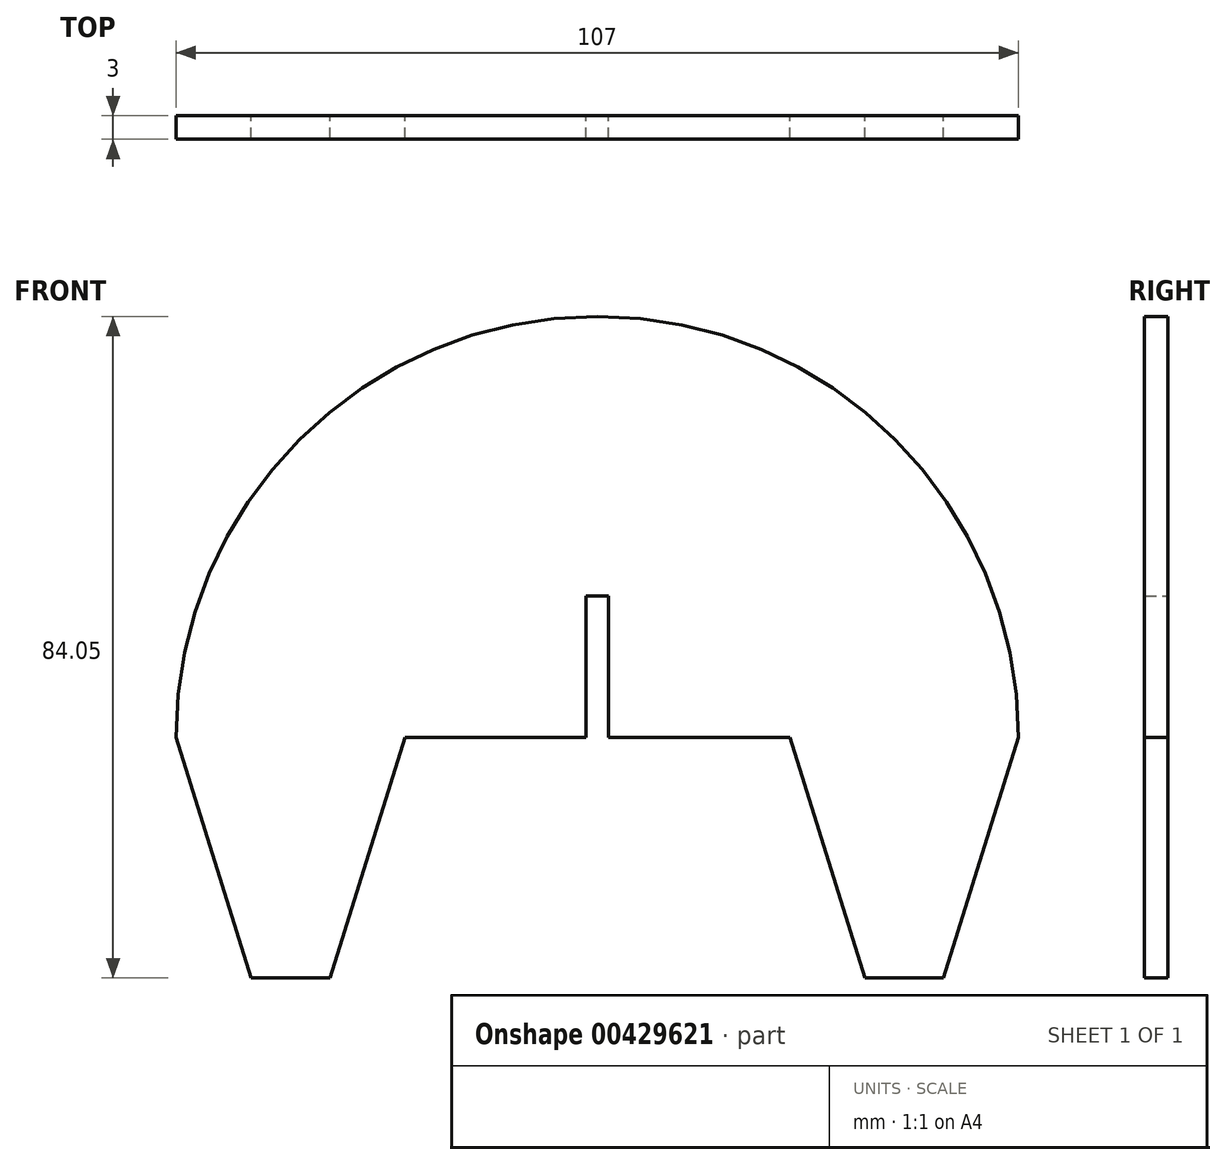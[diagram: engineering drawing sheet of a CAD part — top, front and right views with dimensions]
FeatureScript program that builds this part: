
annotation { "Feature Type Name" : "Feature", "Feature Type Description" : "" }
export const myFeature = defineFeature(function(context is Context, id is Id, definition is map)
    precondition{}
    {
        {
            var Q0;
            Q0=qCreatedBy(makeId("Front.planeOp"),FACE);
            var sketch = newSketch(context, id + "F0", { "sketchPlane" : qUnion([Q0])});
            skArc(sketch, "E0", {"start": v(53.5, 0) * mm, "mid": v(37.83, 37.83) * mm, "end": v(0, 53.5) * mm});
            skLineSegment(sketch, "E1", {"start": v(1.45, 0) * mm, "end": v(24.45, 0) * mm});
            skLineSegment(sketch, "E2.top", {"start": v(0, 18) * mm, "end": v(1.45, 18) * mm});
            skLineSegment(sketch, "E2.right", {"start": v(1.45, 0) * mm, "end": v(1.45, 18) * mm});
            skPoint(sketch, "E3.orphan", {"position": v(-53.5, 0) * mm});
            skPoint(sketch, "E4.start.orphan", {"position": v(24.45, 0) * mm});
            skLineSegment(sketch, "E5", {"start": v(24.45, 0) * mm, "end": v(33.98, -30.55) * mm});
            skLineSegment(sketch, "E6", {"start": v(33.98, -30.55) * mm, "end": v(43.98, -30.55) * mm});
            skLineSegment(sketch, "E7", {"start": v(43.98, -30.55) * mm, "end": v(53.5, 0) * mm});
            skLineSegment(sketch, "E8", {"start": v(1.45, 18) * mm, "end": v(0, 18) * mm});
            skLineSegment(sketch, "E9.MirrorCS", {"start": v(0, 18) * mm, "end": v(-1.45, 18) * mm});
            skLineSegment(sketch, "E10.MirrorCS", {"start": v(-1.45, 18) * mm, "end": v(0, 18) * mm});
            skPoint(sketch, "E11.MirrorP", {"position": v(-24.45, 0) * mm});
            skArc(sketch, "E12.MirrorCS", {"start": v(-53.5, 0) * mm, "mid": v(-37.83, 37.83) * mm, "end": v(0, 53.5) * mm});
            skLineSegment(sketch, "E13.MirrorCS", {"start": v(-24.45, 0) * mm, "end": v(-33.98, -30.55) * mm});
            skLineSegment(sketch, "E14.MirrorCS", {"start": v(-1.45, 0) * mm, "end": v(-1.45, 18) * mm});
            skLineSegment(sketch, "E15.MirrorCS", {"start": v(-1.45, 0) * mm, "end": v(-24.45, 0) * mm});
            skLineSegment(sketch, "E16.MirrorCS", {"start": v(-33.98, -30.55) * mm, "end": v(-43.98, -30.55) * mm});
            skLineSegment(sketch, "E17.MirrorCS", {"start": v(-43.98, -30.55) * mm, "end": v(-53.5, 0) * mm});
            skSolve(sketch);
        }
        {
            var Q0;
            Q0 = qSketchRegion(id + "F0", true);
            extrude(context, id + "F1", {"entities" : qUnion([Q0]), "depth" : 3 * mm});
        }
    });
